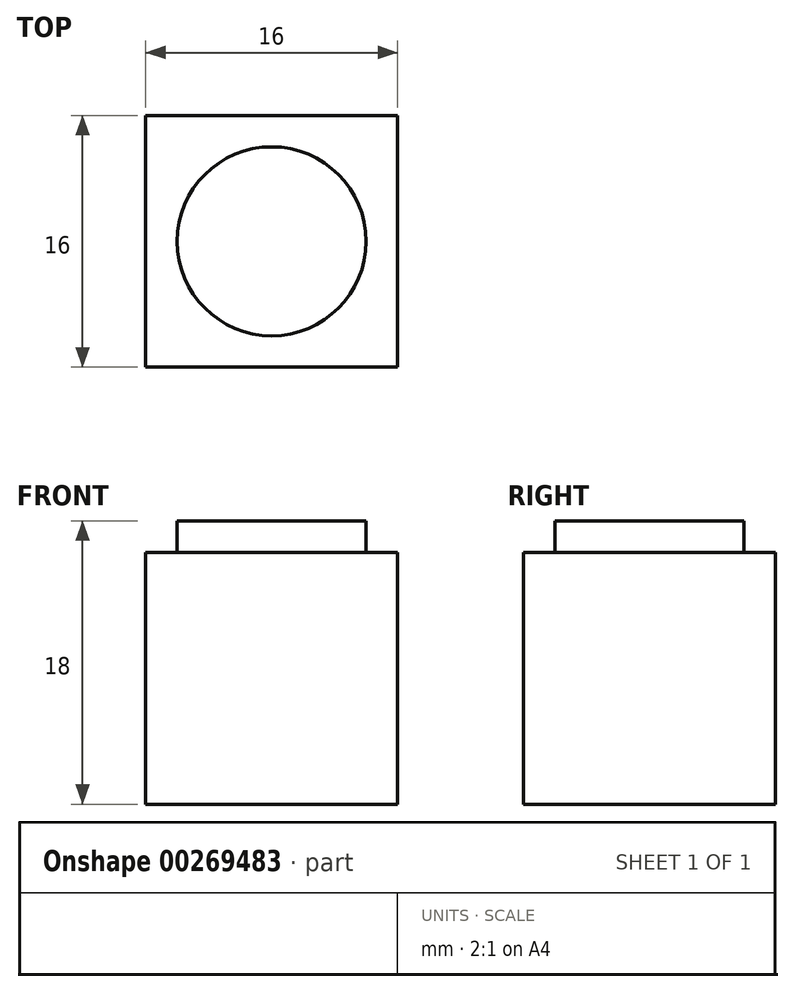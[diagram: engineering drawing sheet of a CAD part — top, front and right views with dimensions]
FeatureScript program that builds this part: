
annotation { "Feature Type Name" : "Feature", "Feature Type Description" : "" }
export const myFeature = defineFeature(function(context is Context, id is Id, definition is map)
    precondition{}
    {
        {
            var Q0;
            Q0=qCreatedBy(makeId("Front.planeOp"),FACE);
            var sketch = newSketch(context, id + "F0", { "sketchPlane" : qUnion([Q0])});
            skLineSegment(sketch, "E0.bottom", {"start": v(-8, 8) * mm, "end": v(8, 8) * mm});
            skLineSegment(sketch, "E0.top", {"start": v(-8, -8) * mm, "end": v(8, -8) * mm});
            skLineSegment(sketch, "E0.left", {"start": v(-8, 8) * mm, "end": v(-8, -8) * mm});
            skLineSegment(sketch, "E0.right", {"start": v(8, 8) * mm, "end": v(8, -8) * mm});
            skPoint(sketch, "E0.middle", {"position": v(0, 0) * mm});
            skSolve(sketch);
        }
        {
            var Q0;
            Q0=makeQuery(id+"F0.imprint","IMPRINT",FACE,{"disambiguationData":[TD([[makeQuery(id+"F0.imprint","IMPRINT",EDGE,{"derivedFrom":sQuery(id+"F0.wireOp",EDGE,"E0.bottom")}),-1.0]])]});
            extrude(context, id + "F1", {"entities" : qUnion([Q0]), "endBound" : BoundingType.SYMMETRIC, "depth" : 16 * mm});
        }
        {
            var Q0;
            Q0=qCreatedBy(makeId("Top.planeOp"),FACE);
            var sketch = newSketch(context, id + "F2", { "sketchPlane" : qUnion([Q0])});
            skCircle(sketch, "E1", {"center": v(0, 0) * mm, "radius": 6 * mm});
            skSolve(sketch);
        }
        {
            var Q0;
            Q0 = qSketchRegion(id + "F2", true);
            extrude(context, id + "F3", {"entities" : qUnion([Q0]), "operationType" : NewBodyOperationType.ADD, "depth" : 10 * mm});
        }
    });
